# Revit family: Ведро педальное для мусора Brabantia
name_source: partatom
category: Оборудование
revit_build: Autodesk Revit 2017 (Build: 20170118_1100(x64)
units: mm (PartAtom-declared; Revit-internal decimal feet)

## family parameters
Всегда вертикально = Да
На основе рабочей плоскости = Нет
Общий = Нет
При загрузке вырезать с полостями = Нет
Размер круглого соединителя = Использовать радиус
Тип детали = Вставляется
Точка расчета площади = Нет

## types (3) — shared parameters
Общ_Единицы измерения = шт.
Общ_Поставщик = Brabantia

## per-type parameters (varying)
| type | 12л | 20л | 5л | Высота | Глубина | Диаметр-10 | До педали | Изготовитель | Общ_Наименование | Радиус | Ширина |
| 12л | Да | Нет | Нет | 410 мм | 250 мм | 240 мм | 110 мм |  | Бак для мусора с внутренним ведром, с педалью, 20л, нержавеющая сталь | 125 мм | 250 мм |
| 5л | Нет | Нет | Да | 290 мм | 205 мм | 195 мм | 87.5 мм |  | Бак для мусора с внутренним ведром, с педалью 5л сталь полированная | 102.5 мм | 205 мм |
| 20л | Нет | Да | Нет | 470 мм | 290 мм | 280 мм | 130 мм | Severin | Ведро для мусора с педалью, 20л, нержавеющая сталь | 145 мм | 290 мм |
